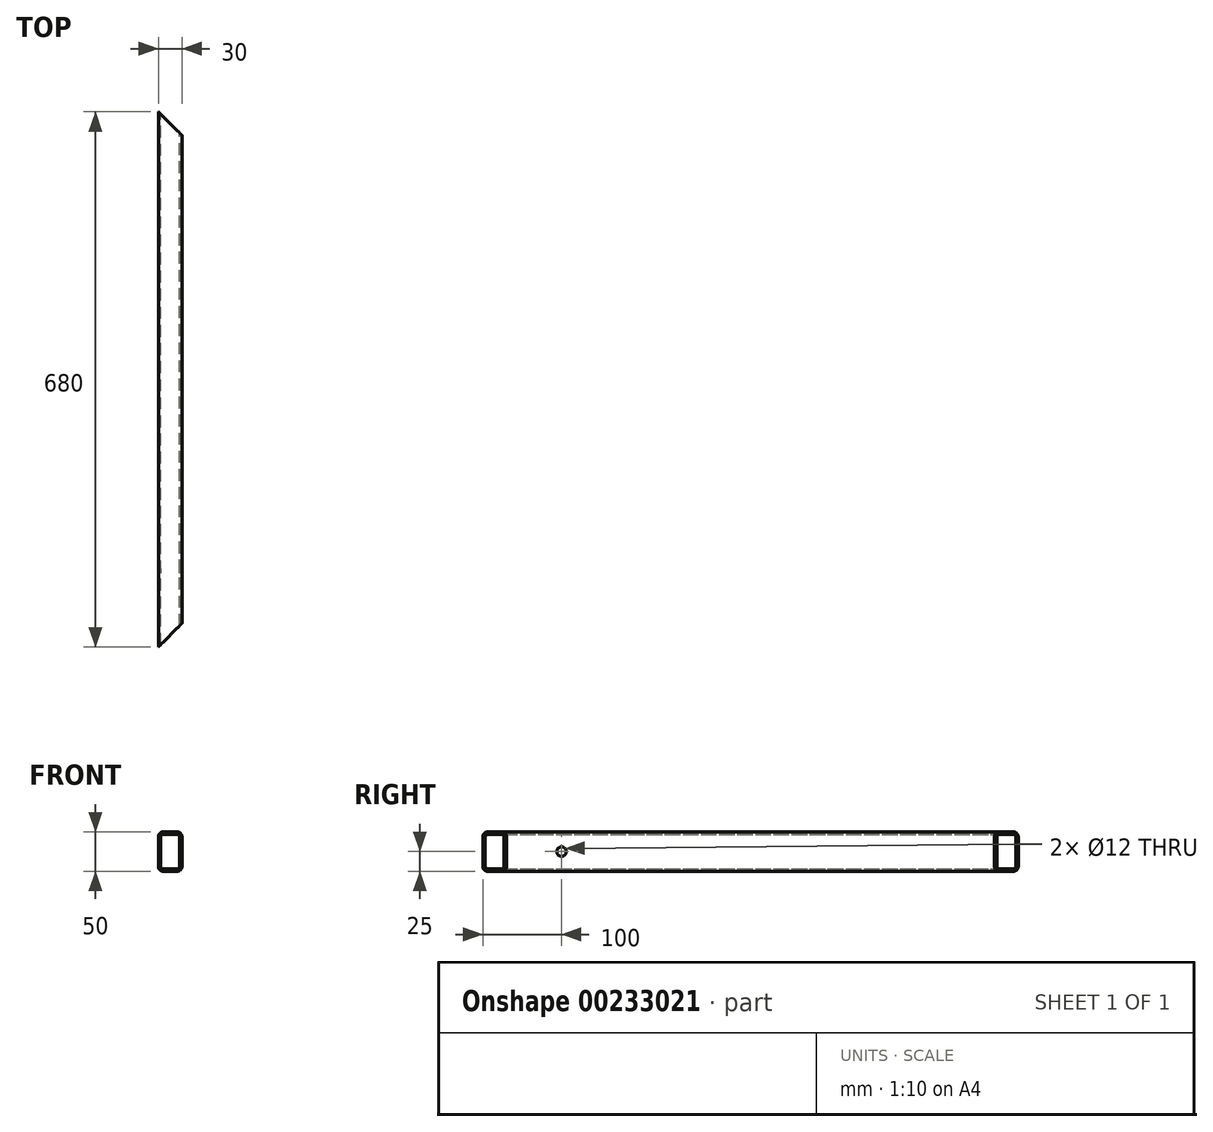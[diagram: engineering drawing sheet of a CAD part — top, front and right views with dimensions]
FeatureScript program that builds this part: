
annotation { "Feature Type Name" : "Feature", "Feature Type Description" : "" }
export const myFeature = defineFeature(function(context is Context, id is Id, definition is map)
    precondition{}
    {
        {
            var Q0;
            Q0=qCreatedBy(makeId("Front.planeOp"),FACE);
            var sketch = newSketch(context, id + "F0", { "sketchPlane" : qUnion([Q0])});
            skLineSegment(sketch, "E0.bottom", {"start": v(9, 25) * mm, "end": v(-9, 25) * mm});
            skLineSegment(sketch, "E0.top", {"start": v(9, -25) * mm, "end": v(-9, -25) * mm});
            skLineSegment(sketch, "E0.left", {"start": v(15, 19) * mm, "end": v(15, -19) * mm});
            skLineSegment(sketch, "E0.right", {"start": v(-15, 19) * mm, "end": v(-15, -19) * mm});
            skPoint(sketch, "E0.middle", {"position": v(0, 0) * mm});
            skPoint(sketch, "E1.visualSharp", {"position": v(-15, 25) * mm});
            skArc(sketch, "E1.filletArc", {"start": v(-9, 25) * mm, "mid": v(-13.24, 23.24) * mm, "end": v(-15, 19) * mm});
            skPoint(sketch, "E2.visualSharp", {"position": v(-15, -25) * mm});
            skArc(sketch, "E2.filletArc", {"start": v(-15, -19) * mm, "mid": v(-13.24, -23.24) * mm, "end": v(-9, -25) * mm});
            skPoint(sketch, "E3.visualSharp", {"position": v(15, -25) * mm});
            skArc(sketch, "E3.filletArc", {"start": v(9, -25) * mm, "mid": v(13.24, -23.24) * mm, "end": v(15, -19) * mm});
            skPoint(sketch, "E4.visualSharp", {"position": v(15, 25) * mm});
            skArc(sketch, "E4.filletArc", {"start": v(15, 19) * mm, "mid": v(13.24, 23.24) * mm, "end": v(9, 25) * mm});
            skLineSegment(sketch, "E5.0", {"start": v(9, 22) * mm, "end": v(-9, 22) * mm});
            skArc(sketch, "E5.1", {"start": v(12, 19) * mm, "mid": v(11.12, 21.12) * mm, "end": v(9, 22) * mm});
            skArc(sketch, "E5.2", {"start": v(-9, 22) * mm, "mid": v(-11.12, 21.12) * mm, "end": v(-12, 19) * mm});
            skLineSegment(sketch, "E5.3", {"start": v(12, 19) * mm, "end": v(12, -19) * mm});
            skLineSegment(sketch, "E5.4", {"start": v(-12, 19) * mm, "end": v(-12, -19) * mm});
            skArc(sketch, "E5.5", {"start": v(-12, -19) * mm, "mid": v(-11.12, -21.12) * mm, "end": v(-9, -22) * mm});
            skLineSegment(sketch, "E5.6", {"start": v(9, -22) * mm, "end": v(-9, -22) * mm});
            skArc(sketch, "E5.7", {"start": v(9, -22) * mm, "mid": v(11.12, -21.12) * mm, "end": v(12, -19) * mm});
            skSolve(sketch);
        }
        {
            var Q0;
            Q0=makeQuery(id+"F0.imprint","IMPRINT",FACE,{"disambiguationData":[TD([[makeQuery(id+"F0.imprint","IMPRINT",EDGE,{"derivedFrom":sQuery(id+"F0.wireOp",EDGE,"E0.bottom")}),1.0]])]});
            extrude(context, id + "F1", {"entities" : qUnion([Q0]), "endBound" : BoundingType.SYMMETRIC, "depth" : 680 * mm});
        }
        {
            var Q0;
            Q0=makeQuery(id+"F1.opExtrude","SWEPT_FACE",FACE,{"disambiguationData":[OSD([sQuery(id+"F0.wireOp",EDGE,"E0.bottom")])]});
            var sketch = newSketch(context, id + "F2", { "sketchPlane" : qUnion([Q0])});
            skLineSegment(sketch, "E6.left", {"start": v(15, 310) * mm, "end": v(15, 340) * mm});
            skPoint(sketch, "E6.middle", {"position": v(0, 340) * mm});
            skLineSegment(sketch, "E7", {"start": v(15, 310) * mm, "end": v(-15, 340) * mm});
            skLineSegment(sketch, "E8", {"start": v(-15, 340) * mm, "end": v(15, 340) * mm});
            skPoint(sketch, "E8.endSnap0", {"position": v(15, 340) * mm});
            skPoint(sketch, "E9.orphan", {"position": v(17.67, 340) * mm});
            skPoint(sketch, "E6.top.end.orphan", {"position": v(-15, 370) * mm});
            skPoint(sketch, "E6.top.start.orphan", {"position": v(15, 370) * mm});
            skPoint(sketch, "E6.right.start.orphan", {"position": v(-15, 310) * mm});
            skLineSegment(sketch, "E10.MirrorCS", {"start": v(-15, -340) * mm, "end": v(15, -340) * mm});
            skPoint(sketch, "E11.MirrorP", {"position": v(17.67, -340) * mm});
            skPoint(sketch, "E12.MirrorP", {"position": v(-15, -310) * mm});
            skLineSegment(sketch, "E13.MirrorCS", {"start": v(15, -310) * mm, "end": v(15, -340) * mm});
            skLineSegment(sketch, "E14.MirrorCS", {"start": v(15, -310) * mm, "end": v(-15, -340) * mm});
            skPoint(sketch, "E15.MirrorP", {"position": v(15, -340) * mm});
            skPoint(sketch, "E16.MirrorP", {"position": v(0, -340) * mm});
            skSolve(sketch);
        }
        {
            var Q0;
            {var subQ0=sQuery(id+"F2.wireOp",EDGE,"E10.MirrorCS");var subQ1=makeQuery(id+"F1.opExtrude","SWEPT_EDGE",EDGE,{"disambiguationData":[OSD([sQuery(id+"F0.wireOp",EDGE,"E0.bottom"),sQuery(id+"F0.wireOp",EDGE,"E1.filletArc")])]});var subQ2=makeQuery(id+"F2.imprint","INTERSECT",VERTEX,{"derivedFrom":[subQ1,subQ0]});var subQ3=sQuery(id+"F2.wireOp",EDGE,"E14.MirrorCS");var subQ4=makeQuery(id+"F2.imprint","INTERSECT",VERTEX,{"derivedFrom":[subQ0,subQ3]});Q0=makeQuery(id+"F2.imprint","IMPRINT",FACE,{"disambiguationData":[TD([[makeQuery(id+"F2.imprint","IMPRINT",EDGE,{"disambiguationData":[TD([[subQ2,1.0],[subQ4,-1.0]])],"derivedFrom":subQ0}),1.0]])]});}
            var Q1;
            {var subQ0=sQuery(id+"F2.wireOp",EDGE,"E10.MirrorCS");var subQ1=sQuery(id+"F0.wireOp",EDGE,"E0.bottom");var subQ2=makeQuery(id+"F1.opExtrude","SWEPT_EDGE",EDGE,{"disambiguationData":[OSD([subQ1,sQuery(id+"F0.wireOp",EDGE,"E4.filletArc")])]});var subQ3=makeQuery(id+"F2.imprint","INTERSECT",VERTEX,{"derivedFrom":[subQ2,subQ0]});var subQ4=makeQuery(id+"F1.opExtrude","SWEPT_EDGE",EDGE,{"disambiguationData":[OSD([subQ1,sQuery(id+"F0.wireOp",EDGE,"E1.filletArc")])]});var subQ5=makeQuery(id+"F2.imprint","INTERSECT",VERTEX,{"derivedFrom":[subQ4,subQ0]});Q1=makeQuery(id+"F2.imprint","IMPRINT",FACE,{"disambiguationData":[TD([[makeQuery(id+"F2.imprint","IMPRINT",EDGE,{"disambiguationData":[TD([[subQ3,-1.0],[subQ5,1.0]])],"derivedFrom":subQ0}),-1.0]])]});}
            var Q2;
            {var subQ3=sQuery(id+"F2.wireOp",EDGE,"E13.MirrorCS");Q2=makeQuery(id+"F2.imprint","IMPRINT",FACE,{"disambiguationData":[TD([[makeQuery(id+"F2.imprint","IMPRINT",EDGE,{"derivedFrom":subQ3}),-1.0]])]});}
            var Q3;
            {var subQ0=sQuery(id+"F2.wireOp",EDGE,"E8");var subQ1=sQuery(id+"F2.wireOp",EDGE,"E7");var subQ2=makeQuery(id+"F2.imprint","INTERSECT",VERTEX,{"derivedFrom":[subQ1,subQ0]});Q3=makeQuery(id+"F2.imprint","IMPRINT",FACE,{"disambiguationData":[TD([[makeQuery(id+"F2.imprint","IMPRINT",EDGE,{"disambiguationData":[TD([[subQ2,1.0]])],"derivedFrom":subQ1}),-1.0]])]});}
            var Q4;
            {var subQ0=sQuery(id+"F2.wireOp",EDGE,"E7");var subQ1=sQuery(id+"F0.wireOp",EDGE,"E0.bottom");var subQ2=makeQuery(id+"F1.opExtrude","SWEPT_EDGE",EDGE,{"disambiguationData":[OSD([subQ1,sQuery(id+"F0.wireOp",EDGE,"E4.filletArc")])]});var subQ3=makeQuery(id+"F2.imprint","INTERSECT",VERTEX,{"derivedFrom":[subQ2,subQ0]});Q4=makeQuery(id+"F2.imprint","IMPRINT",FACE,{"disambiguationData":[TD([[makeQuery(id+"F2.imprint","IMPRINT",EDGE,{"disambiguationData":[TD([[subQ3,-1.0]])],"derivedFrom":subQ0}),-1.0]])]});}
            var Q5;
            {var subQ0=sQuery(id+"F2.wireOp",EDGE,"E6.left");Q5=makeQuery(id+"F2.imprint","IMPRINT",FACE,{"disambiguationData":[TD([[makeQuery(id+"F2.imprint","IMPRINT",EDGE,{"derivedFrom":subQ0}),1.0]])]});}
            var Q6;
            Q6=makeQuery(id+"F1.opExtrude","SWEPT_FACE",FACE,{"disambiguationData":[OSD([sQuery(id+"F0.wireOp",EDGE,"E0.top")])]});
            extrude(context, id + "F3", {"entities" : qUnion([Q0, Q1, Q2, Q3, Q4, Q5]), "operationType" : NewBodyOperationType.REMOVE, "endBound" : BoundingType.UP_TO_SURFACE, "oppositeDirection" : true, "endBoundEntityFace" : qUnion([Q6]), "depth" : 25 * mm});
        }
        {
            var Q0;
            Q0=makeQuery(id+"F1.opExtrude","SWEPT_FACE",FACE,{"disambiguationData":[OSD([sQuery(id+"F0.wireOp",EDGE,"E0.right")])]});
            var sketch = newSketch(context, id + "F4", { "sketchPlane" : qUnion([Q0])});
            skPoint(sketch, "E17", {"position": v(240, 0) * mm});
            skSolve(sketch);
        }
        {
            var Q0;
            Q0=sQuery(id+"F4.wireOp",VERTEX,"546d2ff4-0c5b-4a9e-9d4b-2434e1ea498f");
            var Q1;
            Q1=sQuery(id+"F4.wireOp",VERTEX,"E17");
            var Q2;
            Q2=makeQuery(id+"F1.opExtrude","SWEPT_BODY",BODY,{"disambiguationData":[OSD([sQuery(id+"F0.wireOp",EDGE,"E0.bottom"),sQuery(id+"F0.wireOp",EDGE,"E0.top"),sQuery(id+"F0.wireOp",EDGE,"E0.left"),sQuery(id+"F0.wireOp",EDGE,"E0.right"),sQuery(id+"F0.wireOp",EDGE,"E1.filletArc"),sQuery(id+"F0.wireOp",EDGE,"E2.filletArc"),sQuery(id+"F0.wireOp",EDGE,"E3.filletArc"),sQuery(id+"F0.wireOp",EDGE,"E4.filletArc"),sQuery(id+"F0.wireOp",EDGE,"E5.0"),sQuery(id+"F0.wireOp",EDGE,"E5.1"),sQuery(id+"F0.wireOp",EDGE,"E5.2"),sQuery(id+"F0.wireOp",EDGE,"E5.3"),sQuery(id+"F0.wireOp",EDGE,"E5.4"),sQuery(id+"F0.wireOp",EDGE,"E5.5"),sQuery(id+"F0.wireOp",EDGE,"E5.6"),sQuery(id+"F0.wireOp",EDGE,"E5.7")])]});
            hole(context, id + "F5", {"style" : HoleStyle.SIMPLE, "endStyle" : HoleEndStyle.THROUGH, "holeDiameter" : 12 * mm, "startFromSketch" : true, "locations" : qUnion([Q0, Q1]), "scope" : qUnion([Q2]), "isTappedThrough" : true});
        }
    });
